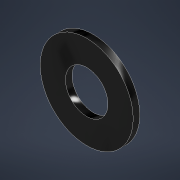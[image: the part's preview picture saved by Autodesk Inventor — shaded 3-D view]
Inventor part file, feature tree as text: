
AUTODESK INVENTOR PART (.ipt)
format: ipt  version: 2022 (Build 260153000, 153)  size: 94,720 bytes
history: native  units: mm
features: extrude x1, sketch x1
ambient origin geometry x8: Origin, YZ Plane, XZ Plane, XY Plane, X Axis, Y Axis, Z Axis, Center Point
bodies: Solid1 (feature_tree)
feature tree (2):
  extrude  "Extrusion1"  Depth=0.5mm
  sketch  "Sketch1"  dims[d0=3.2mm d1=7.0mm d2=0.5mm d3=0.0mm]
